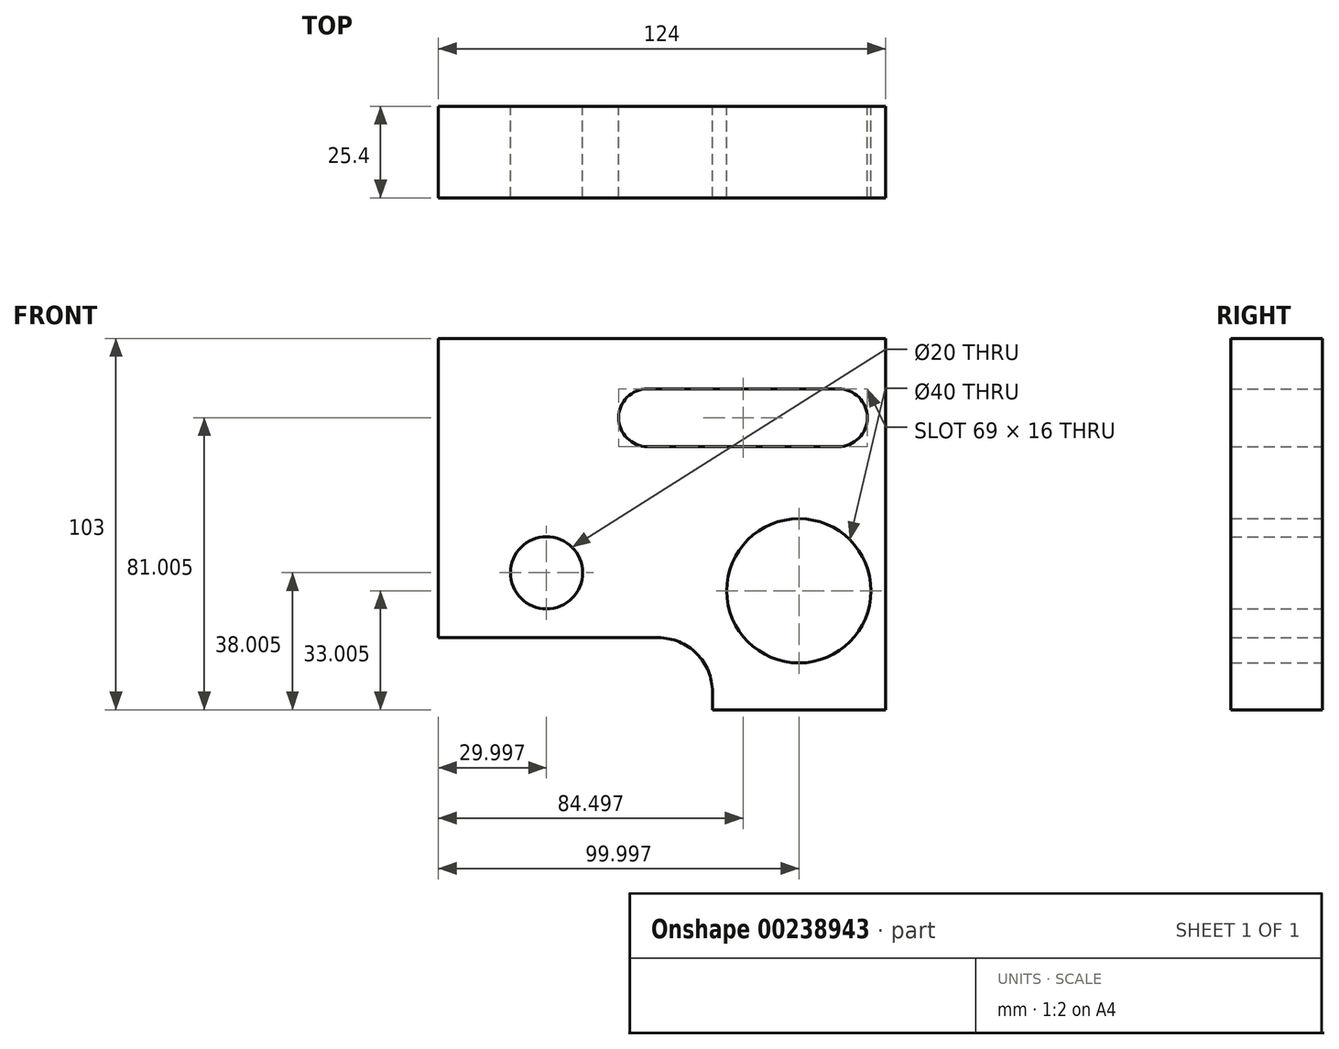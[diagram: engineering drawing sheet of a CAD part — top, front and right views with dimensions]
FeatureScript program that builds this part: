
annotation { "Feature Type Name" : "Feature", "Feature Type Description" : "" }
export const myFeature = defineFeature(function(context is Context, id is Id, definition is map)
    precondition{}
    {
        {
            var Q0;
            Q0=qCreatedBy(makeId("Front.planeOp"),FACE);
            var sketch = newSketch(context, id + "F0", { "sketchPlane" : qUnion([Q0])});
            skLineSegment(sketch, "E0.bottom", {"start": v(-93.14, 76.91) * mm, "end": v(30.86, 76.91) * mm});
            skLineSegment(sketch, "E0.right", {"start": v(30.86, 76.91) * mm, "end": v(30.86, -26.09) * mm});
            skLineSegment(sketch, "E1", {"start": v(-93.14, 76.91) * mm, "end": v(-93.14, -6.09) * mm});
            skLineSegment(sketch, "E2", {"start": v(-93.14, -6.09) * mm, "end": v(-32.13, -6.09) * mm});
            skLineSegment(sketch, "E3", {"start": v(30.86, -26.09) * mm, "end": v(-17.14, -26.09) * mm});
            skLineSegment(sketch, "E4", {"start": v(-17.14, -26.09) * mm, "end": v(-17.13, -21.12) * mm});
            skPoint(sketch, "E5.visualSharp", {"position": v(-17.1, -6.09) * mm});
            skArc(sketch, "E5.filletArc", {"start": v(-17.13, -21.12) * mm, "mid": v(-21.5, -10.5) * mm, "end": v(-32.13, -6.09) * mm});
            skLineSegment(sketch, "E6", {"start": v(-93.14, -6.09) * mm, "end": v(-93.14, 11.91) * mm});
            skLineSegment(sketch, "E7", {"start": v(-93.14, 11.91) * mm, "end": v(-93.14, -6.09) * mm});
            skLineSegment(sketch, "E8", {"start": v(-93.14, -6.09) * mm, "end": v(-64.1, -6.09) * mm});
            skCircle(sketch, "E9", {"center": v(-63.14, 11.91) * mm, "radius": 10 * mm});
            skLineSegment(sketch, "E10", {"start": v(30.86, -26.09) * mm, "end": v(6.86, -26.09) * mm});
            skLineSegment(sketch, "E11", {"start": v(6.86, -26.09) * mm, "end": v(30.86, -26.09) * mm});
            skLineSegment(sketch, "E12", {"start": v(30.86, -26.09) * mm, "end": v(30.86, 6.91) * mm});
            skCircle(sketch, "E13", {"center": v(6.86, 6.91) * mm, "radius": 20 * mm});
            skLineSegment(sketch, "E14", {"start": v(30.86, 76.91) * mm, "end": v(-43.14, 76.91) * mm});
            skLineSegment(sketch, "E15", {"start": v(30.86, 76.91) * mm, "end": v(25.86, 76.91) * mm});
            skLineSegment(sketch, "E16", {"start": v(30.86, 76.91) * mm, "end": v(30.86, 62.91) * mm});
            skLineSegment(sketch, "E17", {"start": v(30.86, 62.91) * mm, "end": v(30.86, 46.91) * mm});
            skLineSegment(sketch, "E18", {"start": v(17.86, 46.91) * mm, "end": v(-35.14, 46.91) * mm});
            skLineSegment(sketch, "E19", {"start": v(-43.14, 54.91) * mm, "end": v(-43.14, 54.91) * mm});
            skLineSegment(sketch, "E20", {"start": v(25.86, 54.91) * mm, "end": v(25.86, 54.91) * mm});
            skArc(sketch, "E21.filletArc", {"start": v(-35.14, 62.91) * mm, "mid": v(-40.8, 60.57) * mm, "end": v(-43.14, 54.91) * mm});
            skPoint(sketch, "E22.visualSharp", {"position": v(-43.14, 46.91) * mm});
            skArc(sketch, "E22.filletArc", {"start": v(-43.14, 54.91) * mm, "mid": v(-40.8, 49.26) * mm, "end": v(-35.14, 46.91) * mm});
            skPoint(sketch, "E23.newPointB", {"position": v(25.86, 46.91) * mm});
            skArc(sketch, "E23.filletArc", {"start": v(17.86, 46.91) * mm, "mid": v(23.51, 49.26) * mm, "end": v(25.86, 54.91) * mm});
            skArc(sketch, "E24.filletArc", {"start": v(25.86, 54.91) * mm, "mid": v(23.51, 60.57) * mm, "end": v(17.86, 62.91) * mm});
            skLineSegment(sketch, "E25", {"start": v(-35.14, 62.91) * mm, "end": v(17.86, 62.91) * mm});
            skSolve(sketch);
        }
        {
            var Q0;
            Q0=makeQuery(id+"F0.imprint","IMPRINT",FACE,{"disambiguationData":[TD([[makeQuery(id+"F0.imprint","IMPRINT",EDGE,{"derivedFrom":sQuery(id+"F0.wireOp",EDGE,"E0.bottom")}),-1.0]])]});
            extrude(context, id + "F1", {"entities" : qUnion([Q0]), "depth" : 25.4 * mm});
        }
    });
